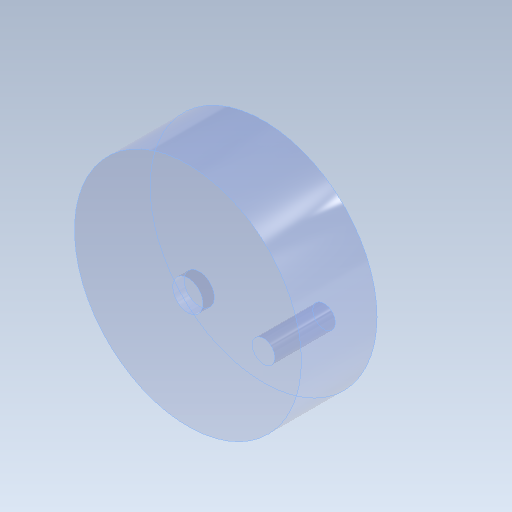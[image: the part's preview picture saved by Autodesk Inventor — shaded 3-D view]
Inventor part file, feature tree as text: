
AUTODESK INVENTOR PART (.ipt)
format: ipt  version: 2021 (Build 250183000, 183)  size: 109,568 bytes
history: native  units: mm
features: extrude x3, sketch x3
ambient origin geometry x8: Origin, YZ Plane, XZ Plane, XY Plane, X Axis, Y Axis, Z Axis, Center Point
bodies: Solid1 (feature_tree)
feature tree (6):
  extrude  "Extrusion1"  Depth=10.0mm TaperAngle=0.0deg
  extrude  "Extrusion2"  Depth=1.5mm TaperAngle=0.0deg
  extrude  "Extrusion3"  Depth=8.0mm TaperAngle=0.0deg
  sketch  "Sketch1"  dims[d0=30.0mm d1=10.0mm d2=0.0mm]
  sketch  "Sketch2"  dims[d3=4.0mm d4=1.5mm d5=0.0mm]
  sketch  "Sketch3"  dims[d6=3.0mm d7=8.0mm d8=0.0mm]
